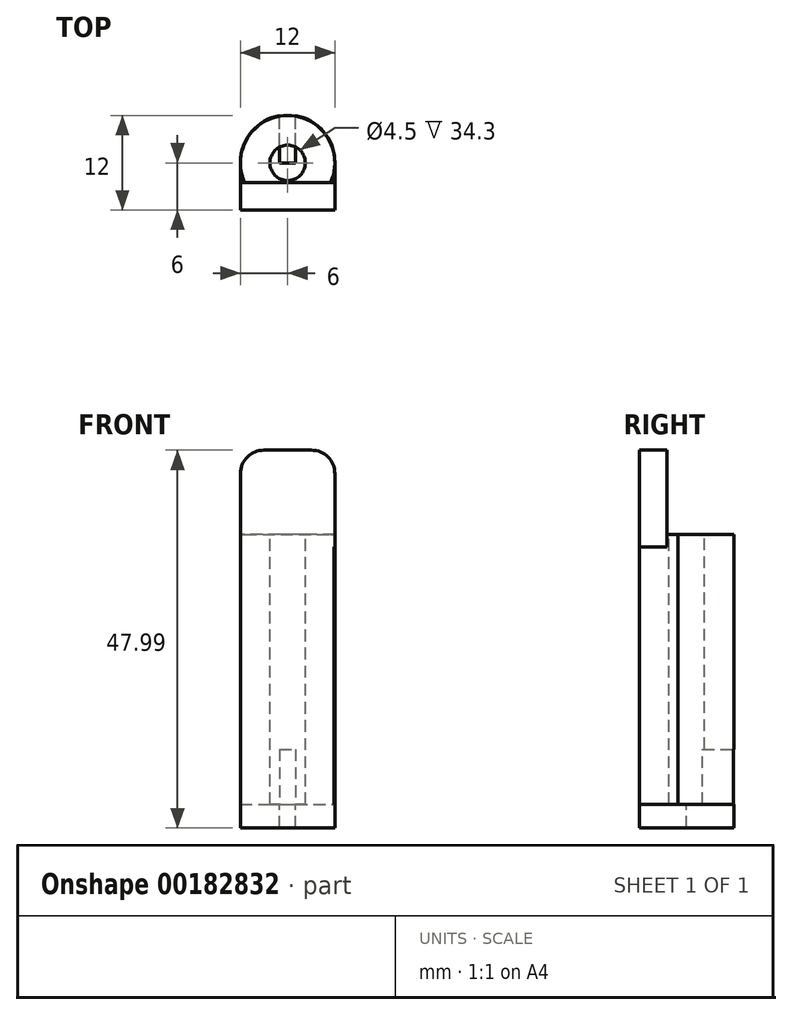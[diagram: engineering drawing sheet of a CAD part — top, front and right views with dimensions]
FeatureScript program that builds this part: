
annotation { "Feature Type Name" : "Feature", "Feature Type Description" : "" }
export const myFeature = defineFeature(function(context is Context, id is Id, definition is map)
    precondition{}
    {
        {
            var Q0;
            Q0=qCreatedBy(makeId("Top.planeOp"),FACE);
            var sketch = newSketch(context, id + "F0", { "sketchPlane" : qUnion([Q0])});
            skCircle(sketch, "E0", {"center": v(0, 0) * mm, "radius": 6 * mm});
            skSolve(sketch);
        }
        {
            var Q0;
            Q0 = qSketchRegion(id + "F0", true);
            extrude(context, id + "F1", {"entities" : qUnion([Q0]), "depth" : 37.3 * mm});
        }
        {
            var Q0;
            Q0=makeQuery(id+"F1.opExtrude","CAP_FACE",FACE,{"disambiguationData":[OSD([sQuery(id+"F0.wireOp",EDGE,"E0")])],"isStart":true});
            var sketch = newSketch(context, id + "F2", { "sketchPlane" : qUnion([Q0])});
            skLineSegment(sketch, "E1.bottom", {"start": v(-6, 6) * mm, "end": v(6, 6) * mm});
            skLineSegment(sketch, "E1.top", {"start": v(-6, -6) * mm, "end": v(6, -6) * mm});
            skLineSegment(sketch, "E1.left", {"start": v(-6, 6) * mm, "end": v(-6, -6) * mm});
            skLineSegment(sketch, "E1.right", {"start": v(6, 6) * mm, "end": v(6, -6) * mm});
            skSolve(sketch);
        }
        {
            var Q0;
            Q0 = qSketchRegion(id + "F2", true);
            extrude(context, id + "F3", {"entities" : qUnion([Q0]), "operationType" : NewBodyOperationType.ADD, "oppositeDirection" : true, "depth" : 3 * mm});
        }
        {
            var Q0;
            Q0=makeQuery(id+"F3.opExtrude","SWEPT_FACE",FACE,{"disambiguationData":[OSD([sQuery(id+"F2.wireOp",EDGE,"E1.bottom")])]});
            var sketch = newSketch(context, id + "F4", { "sketchPlane" : qUnion([Q0])});
            skLineSegment(sketch, "E2.bottom", {"start": v(-6, 48) * mm, "end": v(6, 48) * mm});
            skLineSegment(sketch, "E2.top", {"start": v(-6, 35.69) * mm, "end": v(6, 35.69) * mm});
            skLineSegment(sketch, "E2.left", {"start": v(-6, 48) * mm, "end": v(-6, 35.69) * mm});
            skLineSegment(sketch, "E2.right", {"start": v(6, 48) * mm, "end": v(6, 35.69) * mm});
            skSolve(sketch);
        }
        {
            var Q0;
            Q0 = qSketchRegion(id + "F4", true);
            extrude(context, id + "F5", {"entities" : qUnion([Q0]), "operationType" : NewBodyOperationType.ADD, "oppositeDirection" : true, "depth" : 3.5 * mm});
        }
        {
            var Q0;
            Q0=makeQuery(id+"F3.opExtrude","SWEPT_FACE",FACE,{"disambiguationData":[OSD([sQuery(id+"F2.wireOp",EDGE,"E1.top")])]});
            var sketch = newSketch(context, id + "F6", { "sketchPlane" : qUnion([Q0])});
            skLineSegment(sketch, "E3.bottom", {"start": v(-1, 0) * mm, "end": v(1, 0) * mm});
            skLineSegment(sketch, "E3.top", {"start": v(-1, 10) * mm, "end": v(1, 10) * mm});
            skLineSegment(sketch, "E3.left", {"start": v(-1, 0) * mm, "end": v(-1, 10) * mm});
            skLineSegment(sketch, "E3.right", {"start": v(1, 0) * mm, "end": v(1, 10) * mm});
            skSolve(sketch);
        }
        {
            var Q0;
            Q0 = qSketchRegion(id + "F6", true);
            extrude(context, id + "F7", {"entities" : qUnion([Q0]), "operationType" : NewBodyOperationType.REMOVE, "oppositeDirection" : true, "depth" : 6 * mm});
        }
        {
            var Q0;
            Q0=makeQuery(id+"F3.opExtrude","SWEPT_EDGE",EDGE,{"disambiguationData":[OSD([sQuery(id+"F2.wireOp",EDGE,"E1.top"),sQuery(id+"F2.wireOp",EDGE,"E1.left")])]});
            var Q1;
            Q1=makeQuery(id+"F3.opExtrude","SWEPT_EDGE",EDGE,{"disambiguationData":[OSD([sQuery(id+"F2.wireOp",EDGE,"E1.top"),sQuery(id+"F2.wireOp",EDGE,"E1.right")])]});
            fillet(context, id + "F8", {"entities" : qUnion([Q0, Q1]), "radius" : 6 * mm, "tangentPropagation" : true, "allowEdgeOverflow" : false});
        }
        {
            var Q0;
            Q0=makeQuery(id+"F3.opExtrude","SWEPT_FACE",FACE,{"disambiguationData":[OSD([sQuery(id+"F2.wireOp",EDGE,"E1.bottom")])]});
            var sketch = newSketch(context, id + "F9", { "sketchPlane" : qUnion([Q0])});
            skLineSegment(sketch, "E4.bottom", {"start": v(-6, 3) * mm, "end": v(5.9, 3) * mm});
            skLineSegment(sketch, "E4.top", {"start": v(-6, 37.25) * mm, "end": v(5.9, 37.25) * mm});
            skLineSegment(sketch, "E4.left", {"start": v(-6, 3) * mm, "end": v(-6, 37.25) * mm});
            skLineSegment(sketch, "E4.right", {"start": v(5.9, 3) * mm, "end": v(5.9, 37.25) * mm});
            skSolve(sketch);
        }
        {
            var Q0;
            Q0 = qSketchRegion(id + "F9", true);
            extrude(context, id + "F10", {"entities" : qUnion([Q0]), "operationType" : NewBodyOperationType.ADD, "oppositeDirection" : true, "depth" : 6 * mm});
        }
        {
            var Q0;
            Q0=makeQuery(id+"F1.opExtrude","CAP_FACE",FACE,{"disambiguationData":[OSD([sQuery(id+"F0.wireOp",EDGE,"E0")])],"isStart":false});
            var sketch = newSketch(context, id + "F11", { "sketchPlane" : qUnion([Q0])});
            skCircle(sketch, "E5", {"center": v(0, 0) * mm, "radius": 2.25 * mm});
            skSolve(sketch);
        }
        {
            var Q0;
            Q0 = qSketchRegion(id + "F11", true);
            extrude(context, id + "F12", {"entities" : qUnion([Q0]), "operationType" : NewBodyOperationType.REMOVE, "oppositeDirection" : true, "depth" : 34.3 * mm});
        }
        {
            var Q0;
            Q0=makeQuery(id+"F5.opExtrude","SWEPT_EDGE",EDGE,{"disambiguationData":[OSD([sQuery(id+"F4.wireOp",EDGE,"E2.bottom"),sQuery(id+"F4.wireOp",EDGE,"E2.right")])]});
            var Q1;
            Q1=makeQuery(id+"F5.opExtrude","SWEPT_EDGE",EDGE,{"disambiguationData":[OSD([sQuery(id+"F4.wireOp",EDGE,"E2.bottom"),sQuery(id+"F4.wireOp",EDGE,"E2.left")])]});
            fillet(context, id + "F13", {"entities" : qUnion([Q0, Q1]), "radius" : 3 * mm, "tangentPropagation" : true, "allowEdgeOverflow" : false});
        }
    });
